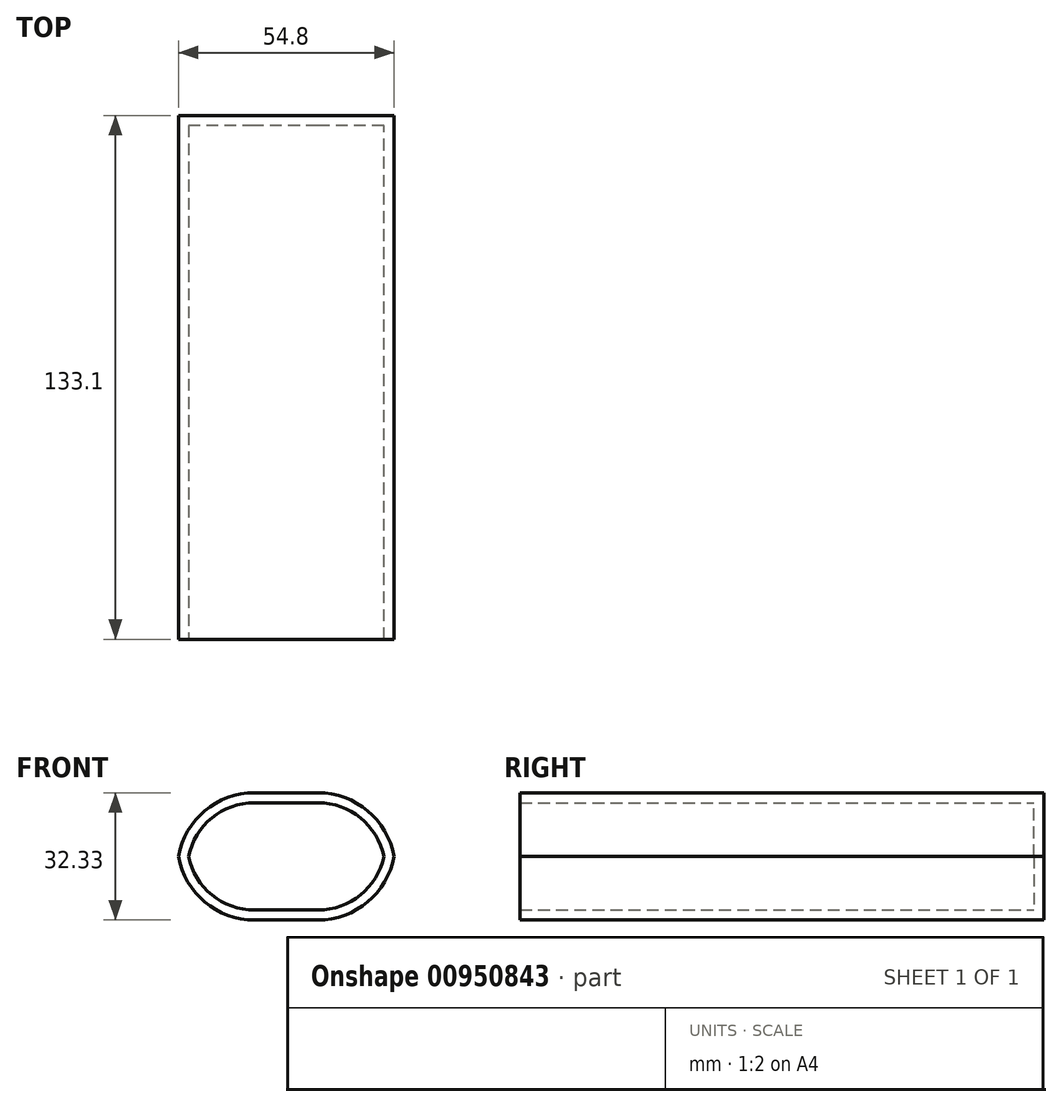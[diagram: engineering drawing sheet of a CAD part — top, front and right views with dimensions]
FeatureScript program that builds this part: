
annotation { "Feature Type Name" : "Feature", "Feature Type Description" : "" }
export const myFeature = defineFeature(function(context is Context, id is Id, definition is map)
    precondition{}
    {
        {
            var Q0;
            Q0=qCreatedBy(makeId("Front.planeOp"),FACE);
            var sketch = newSketch(context, id + "F0", { "sketchPlane" : qUnion([Q0])});
            skLineSegment(sketch, "E0.bottom", {"start": v(0, 0) * mm, "end": v(-55.42, 0) * mm});
            skLineSegment(sketch, "E0.top", {"start": v(0, 32.33) * mm, "end": v(-55.42, 32.33) * mm});
            skLineSegment(sketch, "E0.left", {"start": v(0, 0) * mm, "end": v(0, 32.33) * mm});
            skLineSegment(sketch, "E0.right", {"start": v(-55.42, 0) * mm, "end": v(-55.42, 32.33) * mm});
            skSolve(sketch);
        }
        {
            var Q0;
            Q0=makeQuery(id+"F0.imprint","IMPRINT",FACE,{"disambiguationData":[TD([[makeQuery(id+"F0.imprint","IMPRINT",EDGE,{"derivedFrom":sQuery(id+"F0.wireOp",EDGE,"E0.bottom")}),-1.0]])]});
            extrude(context, id + "F1", {"entities" : qUnion([Q0]), "depth" : 133.1 * mm, "offsetDistance" : 25.4 * mm});
        }
        {
            var Q0;
            Q0=makeQuery(id+"F1.opExtrude","SWEPT_EDGE",EDGE,{"disambiguationData":[OSD([sQuery(id+"F0.wireOp",EDGE,"E0.top"),sQuery(id+"F0.wireOp",EDGE,"E0.right")])]});
            var Q1;
            Q1=makeQuery(id+"F1.opExtrude","SWEPT_EDGE",EDGE,{"disambiguationData":[OSD([sQuery(id+"F0.wireOp",EDGE,"E0.top"),sQuery(id+"F0.wireOp",EDGE,"E0.left")])]});
            var Q2;
            Q2=makeQuery(id+"F1.opExtrude","SWEPT_EDGE",EDGE,{"disambiguationData":[OSD([sQuery(id+"F0.wireOp",EDGE,"E0.bottom"),sQuery(id+"F0.wireOp",EDGE,"E0.left")])]});
            var Q3;
            Q3=makeQuery(id+"F1.opExtrude","SWEPT_EDGE",EDGE,{"disambiguationData":[OSD([sQuery(id+"F0.wireOp",EDGE,"E0.bottom"),sQuery(id+"F0.wireOp",EDGE,"E0.right")])]});
            fillet(context, id + "F2", {"entities" : qUnion([Q0, Q1, Q2, Q3]), "radius" : 19.62 * mm, "tangentPropagation" : true, "allowEdgeOverflow" : false});
        }
        {
            var Q0;
            Q0=makeQuery(id+"F1.opExtrude","CAP_FACE",FACE,{"disambiguationData":[OSD([sQuery(id+"F0.wireOp",EDGE,"E0.bottom"),sQuery(id+"F0.wireOp",EDGE,"E0.top"),sQuery(id+"F0.wireOp",EDGE,"E0.left"),sQuery(id+"F0.wireOp",EDGE,"E0.right")])],"isStart":false});
            shell(context, id + "F3", {"entities" : qUnion([Q0]), "thickness" : 2.54 * mm});
        }
    });
